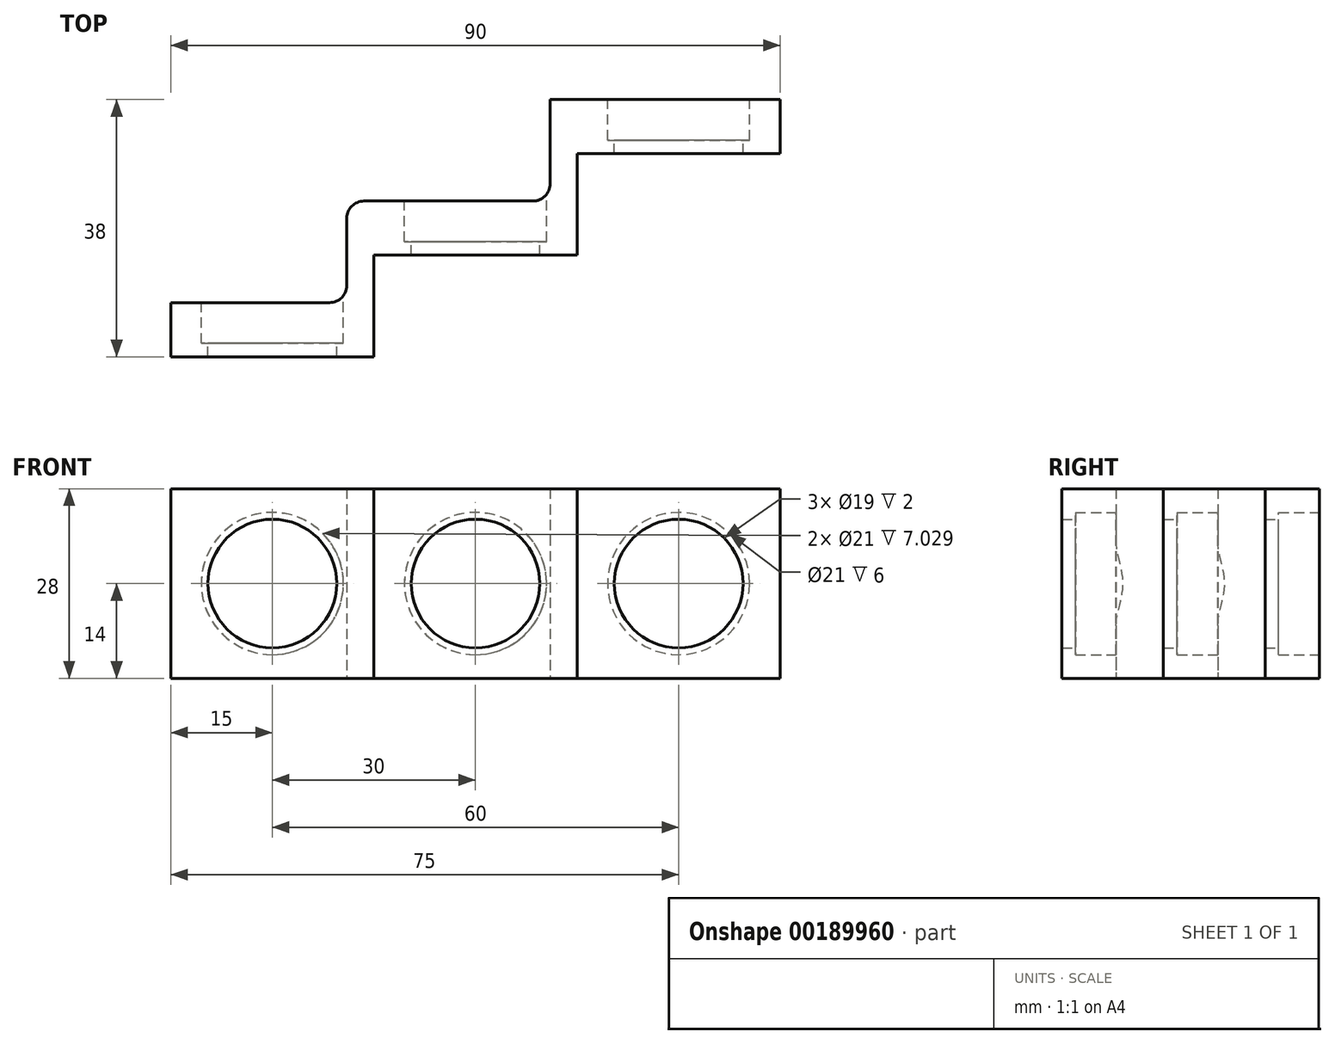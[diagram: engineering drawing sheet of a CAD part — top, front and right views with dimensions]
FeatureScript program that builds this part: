
annotation { "Feature Type Name" : "Feature", "Feature Type Description" : "" }
export const myFeature = defineFeature(function(context is Context, id is Id, definition is map)
    precondition{}
    {
        {
            var Q0;
            Q0=qCreatedBy(makeId("Front.planeOp"),FACE);
            var sketch = newSketch(context, id + "F0", { "sketchPlane" : qUnion([Q0])});
            skLineSegment(sketch, "E0", {"start": v(0, 0) * mm, "end": v(80.9, 0) * mm, "construction": true});
            skCircle(sketch, "E1", {"center": v(0, 0) * mm, "radius": 10.5 * mm});
            skCircle(sketch, "E2.1.0.0", {"center": v(30, 0) * mm, "radius": 10.5 * mm});
            skCircle(sketch, "E2.2.0.0", {"center": v(60, 0) * mm, "radius": 10.5 * mm});
            skLineSegment(sketch, "E2.direction1", {"start": v(0, 0) * mm, "end": v(30, 0) * mm, "construction": true});
            skLineSegment(sketch, "E3.bottom", {"start": v(15, -14) * mm, "end": v(-15, -14) * mm});
            skLineSegment(sketch, "E3.top", {"start": v(15, 14) * mm, "end": v(-15, 14) * mm});
            skLineSegment(sketch, "E3.left", {"start": v(15, -14) * mm, "end": v(15, 14) * mm});
            skLineSegment(sketch, "E3.right", {"start": v(-15, -14) * mm, "end": v(-15, 14) * mm});
            skLineSegment(sketch, "E4.bottom", {"start": v(15, -14) * mm, "end": v(45, -14) * mm});
            skLineSegment(sketch, "E4.top", {"start": v(15, 14) * mm, "end": v(45, 14) * mm});
            skLineSegment(sketch, "E4.right", {"start": v(45, -14) * mm, "end": v(45, 14) * mm});
            skLineSegment(sketch, "E5.bottom", {"start": v(45, -14) * mm, "end": v(75, -14) * mm});
            skLineSegment(sketch, "E5.top", {"start": v(45, 14) * mm, "end": v(75, 14) * mm});
            skLineSegment(sketch, "E5.right", {"start": v(75, -14) * mm, "end": v(75, 14) * mm});
            skCircle(sketch, "E6", {"center": v(0, 0) * mm, "radius": 9.5 * mm});
            skCircle(sketch, "E7.1.0.0", {"center": v(30, 0) * mm, "radius": 9.5 * mm});
            skCircle(sketch, "E7.2.0.0", {"center": v(60, 0) * mm, "radius": 9.5 * mm});
            skSolve(sketch);
        }
        {
            var Q0;
            Q0=makeQuery(id+"F0.imprint","IMPRINT",FACE,{"disambiguationData":[TD([[makeQuery(id+"F0.imprint","IMPRINT",EDGE,{"derivedFrom":sQuery(id+"F0.wireOp",EDGE,"E1")}),1.0]])]});
            var Q1;
            Q1=makeQuery(id+"F0.imprint","IMPRINT",FACE,{"disambiguationData":[TD([[makeQuery(id+"F0.imprint","IMPRINT",EDGE,{"derivedFrom":sQuery(id+"F0.wireOp",EDGE,"E2.2.0.0")}),1.0]])]});
            var Q2;
            Q2=makeQuery(id+"F0.imprint","IMPRINT",FACE,{"disambiguationData":[TD([[makeQuery(id+"F0.imprint","IMPRINT",EDGE,{"derivedFrom":sQuery(id+"F0.wireOp",EDGE,"E2.2.0.0")}),-1.0]])]});
            var Q3;
            Q3=makeQuery(id+"F0.imprint","IMPRINT",FACE,{"disambiguationData":[TD([[makeQuery(id+"F0.imprint","IMPRINT",EDGE,{"derivedFrom":sQuery(id+"F0.wireOp",EDGE,"E2.1.0.0")}),1.0]])]});
            var Q4;
            Q4=makeQuery(id+"F0.imprint","IMPRINT",FACE,{"disambiguationData":[TD([[makeQuery(id+"F0.imprint","IMPRINT",EDGE,{"derivedFrom":sQuery(id+"F0.wireOp",EDGE,"E2.1.0.0")}),-1.0]])]});
            var Q5;
            Q5=makeQuery(id+"F0.imprint","IMPRINT",FACE,{"disambiguationData":[TD([[makeQuery(id+"F0.imprint","IMPRINT",EDGE,{"derivedFrom":sQuery(id+"F0.wireOp",EDGE,"E1")}),-1.0]])]});
            extrude(context, id + "F1", {"entities" : qUnion([Q0, Q1, Q2, Q3, Q4, Q5]), "depth" : 8 * mm});
        }
        {
            var Q0;
            Q0=makeQuery(id+"F0.imprint","IMPRINT",FACE,{"disambiguationData":[TD([[makeQuery(id+"F0.imprint","IMPRINT",EDGE,{"derivedFrom":sQuery(id+"F0.wireOp",EDGE,"E1")}),-1.0]])]});
            var Q1;
            Q1=makeQuery(id+"F0.imprint","IMPRINT",FACE,{"disambiguationData":[TD([[makeQuery(id+"F0.imprint","IMPRINT",EDGE,{"derivedFrom":sQuery(id+"F0.wireOp",EDGE,"E1")}),1.0]])]});
            extrude(context, id + "F2", {"entities" : qUnion([Q0, Q1]), "operationType" : NewBodyOperationType.ADD, "depth" : 8 * mm + 15 * mm + 15 * mm});
        }
        {
            var Q0;
            Q0=makeQuery(id+"F0.imprint","IMPRINT",FACE,{"disambiguationData":[TD([[makeQuery(id+"F0.imprint","IMPRINT",EDGE,{"derivedFrom":sQuery(id+"F0.wireOp",EDGE,"E2.1.0.0")}),1.0]])]});
            var Q1;
            Q1=makeQuery(id+"F0.imprint","IMPRINT",FACE,{"disambiguationData":[TD([[makeQuery(id+"F0.imprint","IMPRINT",EDGE,{"derivedFrom":sQuery(id+"F0.wireOp",EDGE,"E2.1.0.0")}),-1.0]])]});
            extrude(context, id + "F3", {"entities" : qUnion([Q0, Q1]), "operationType" : NewBodyOperationType.ADD, "depth" : 8 * mm + 15 * mm});
        }
        {
            var Q0;
            Q0=makeQuery(id+"F0.imprint","IMPRINT",FACE,{"disambiguationData":[TD([[makeQuery(id+"F0.imprint","IMPRINT",EDGE,{"derivedFrom":sQuery(id+"F0.wireOp",EDGE,"E1")}),1.0]])]});
            extrude(context, id + "F4", {"entities" : qUnion([Q0]), "operationType" : NewBodyOperationType.REMOVE, "depth" : 8 * mm + 15 * mm + 13 * mm});
        }
        {
            var Q0;
            Q0=makeQuery(id+"F0.imprint","IMPRINT",FACE,{"disambiguationData":[TD([[makeQuery(id+"F0.imprint","IMPRINT",EDGE,{"derivedFrom":sQuery(id+"F0.wireOp",EDGE,"E2.1.0.0")}),1.0]])]});
            extrude(context, id + "F5", {"entities" : qUnion([Q0]), "operationType" : NewBodyOperationType.REMOVE, "depth" : 8 * mm + 13 * mm});
        }
        {
            var Q0;
            Q0=makeQuery(id+"F0.imprint","IMPRINT",FACE,{"disambiguationData":[TD([[makeQuery(id+"F0.imprint","IMPRINT",EDGE,{"derivedFrom":sQuery(id+"F0.wireOp",EDGE,"E2.2.0.0")}),1.0]])]});
            extrude(context, id + "F6", {"entities" : qUnion([Q0]), "operationType" : NewBodyOperationType.REMOVE, "depth" : 6 * mm});
        }
        {
            var Q0;
            {var subQ0=sQuery(id+"F0.wireOp",EDGE,"E4.bottom");var subQ1=sQuery(id+"F0.wireOp",EDGE,"E3.bottom");Q0=makeQuery(id+"F3.boolean.opBoolean","MERGE",FACE,{"derivedFrom":[makeQuery(id+"F2.boolean.opBoolean","MERGE",FACE,{"derivedFrom":[makeQuery(id+"F1.opExtrude","SWEPT_FACE",FACE,{"disambiguationData":[OSD([subQ1,subQ0,sQuery(id+"F0.wireOp",EDGE,"E5.bottom")])]}),makeQuery(id+"F2.opExtrude","SWEPT_FACE",FACE,{"disambiguationData":[OSD([subQ1])]})]}),makeQuery(id+"F3.opExtrude","SWEPT_FACE",FACE,{"disambiguationData":[OSD([subQ0])]})]});}
            var sketch = newSketch(context, id + "F7", { "sketchPlane" : qUnion([Q0])});
            skLineSegment(sketch, "E8", {"start": v(-15, 30) * mm, "end": v(8.46, 30) * mm});
            skLineSegment(sketch, "E9", {"start": v(11, 27.46) * mm, "end": v(11, 17.54) * mm});
            skLineSegment(sketch, "E10", {"start": v(13.54, 15) * mm, "end": v(38.46, 15) * mm});
            skLineSegment(sketch, "E11", {"start": v(41, 12.46) * mm, "end": v(41, 0) * mm});
            skLineSegment(sketch, "E12", {"start": v(-15, 30) * mm, "end": v(-15, 0) * mm});
            skLineSegment(sketch, "E13", {"start": v(-15, 0) * mm, "end": v(41, 0) * mm});
            skPoint(sketch, "E14.visualSharp", {"position": v(11, 30) * mm});
            skArc(sketch, "E14.filletArc", {"start": v(11, 27.46) * mm, "mid": v(10.26, 29.26) * mm, "end": v(8.46, 30) * mm});
            skPoint(sketch, "E15.visualSharp", {"position": v(41, 15) * mm});
            skArc(sketch, "E15.filletArc", {"start": v(41, 12.46) * mm, "mid": v(40.26, 14.26) * mm, "end": v(38.46, 15) * mm});
            skPoint(sketch, "E16.visualSharp", {"position": v(11, 15) * mm});
            skArc(sketch, "E16.filletArc", {"start": v(11, 17.54) * mm, "mid": v(11.74, 15.74) * mm, "end": v(13.54, 15) * mm});
            skSolve(sketch);
        }
        {
            var Q0;
            Q0 = qSketchRegion(id + "F7", true);
            extrude(context, id + "F8", {"entities" : qUnion([Q0]), "operationType" : NewBodyOperationType.REMOVE, "endBound" : BoundingType.THROUGH_ALL, "oppositeDirection" : true, "depth" : 25.4 * mm});
        }
    });
